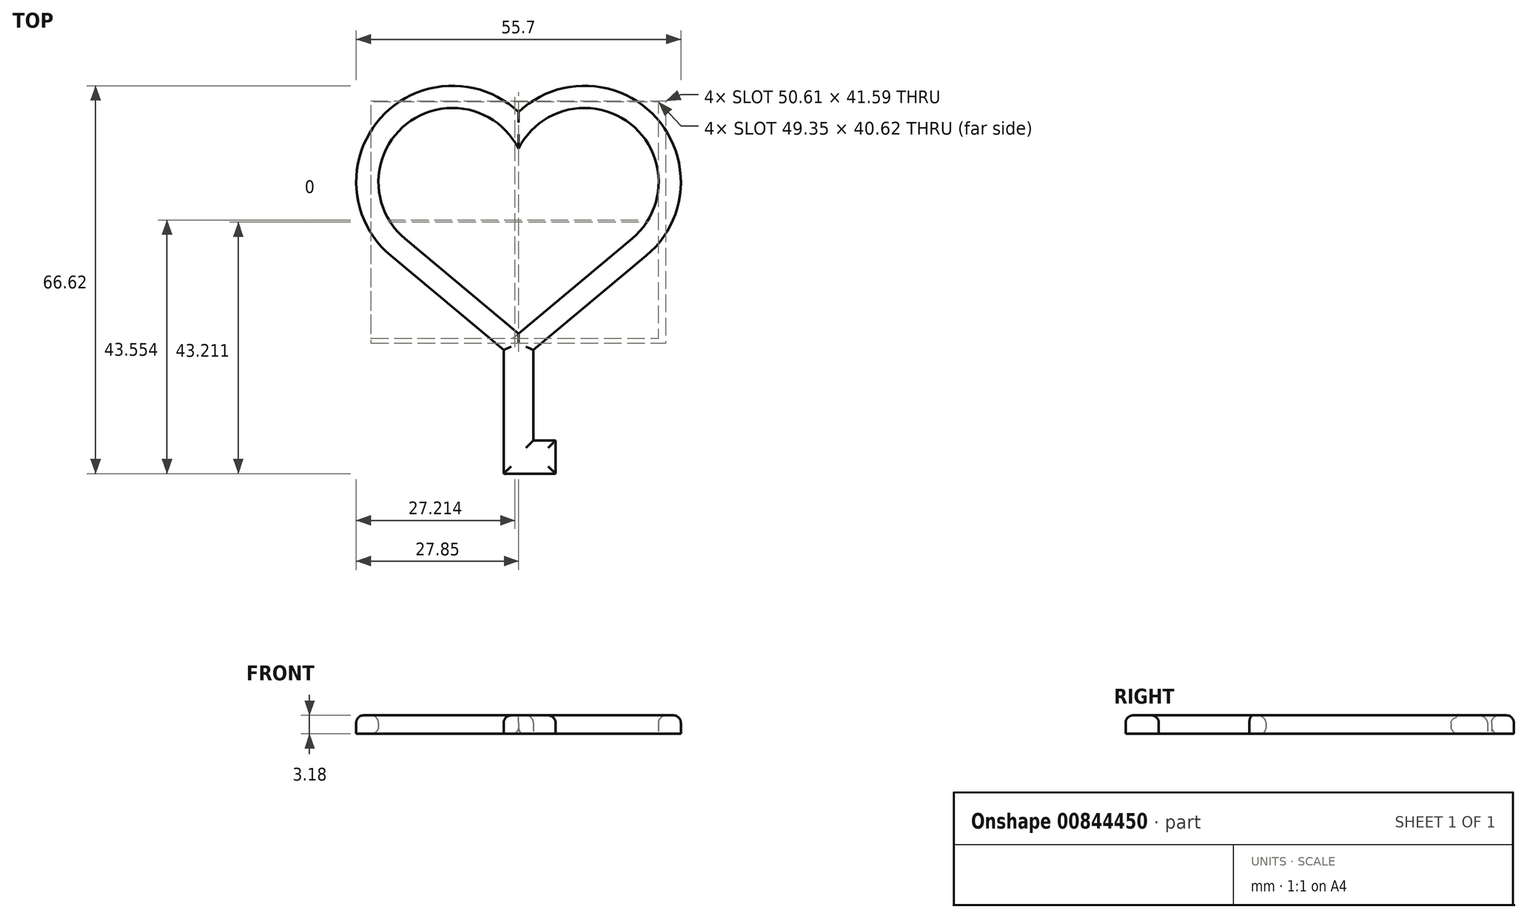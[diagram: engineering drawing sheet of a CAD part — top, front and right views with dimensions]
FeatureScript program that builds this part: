
annotation { "Feature Type Name" : "Feature", "Feature Type Description" : "" }
export const myFeature = defineFeature(function(context is Context, id is Id, definition is map)
    precondition{}
    {
        {
            var Q0;
            Q0=qCreatedBy(makeId("Top.planeOp"),FACE);
            var sketch = newSketch(context, id + "F0", { "sketchPlane" : qUnion([Q0])});
            skLineSegment(sketch, "E0", {"start": v(0, 0) * mm, "end": v(-19.49, 16.3) * mm});
            skLineSegment(sketch, "E1", {"start": v(0, 0) * mm, "end": v(19.49, 16.3) * mm});
            skArc(sketch, "E2", {"start": v(-19.49, 16.3) * mm, "mid": v(-19.23, 35.98) * mm, "end": v(0, 31.75) * mm});
            skArc(sketch, "E3", {"start": v(19.49, 16.3) * mm, "mid": v(19.23, 35.98) * mm, "end": v(0, 31.75) * mm});
            skLineSegment(sketch, "E4", {"start": v(0, 0) * mm, "end": v(0, 31.75) * mm, "construction": true});
            skLineSegment(sketch, "E5", {"start": v(-2.54, -2.84) * mm, "end": v(-2.54, -18.38) * mm});
            skLineSegment(sketch, "E6", {"start": v(-2.54, -24.07) * mm, "end": v(2.54, -24.07) * mm});
            skLineSegment(sketch, "E7", {"start": v(2.54, -18.38) * mm, "end": v(2.54, -2.84) * mm});
            skLineSegment(sketch, "E8.bottom", {"start": v(2.54, -24.07) * mm, "end": v(6.35, -24.07) * mm});
            skLineSegment(sketch, "E8.top", {"start": v(2.54, -18.38) * mm, "end": v(6.35, -18.38) * mm});
            skLineSegment(sketch, "E8.left", {"start": v(-2.54, -24.07) * mm, "end": v(-2.54, -18.38) * mm});
            skLineSegment(sketch, "E8.right", {"start": v(6.35, -24.07) * mm, "end": v(6.35, -18.38) * mm});
            skArc(sketch, "E9.0", {"start": v(-21.93, 13.37) * mm, "mid": v(-23.68, 37) * mm, "end": v(0, 38.03) * mm});
            skLineSegment(sketch, "E9.1", {"start": v(-2.54, -2.84) * mm, "end": v(-21.93, 13.37) * mm});
            skLineSegment(sketch, "E9.2", {"start": v(2.54, -2.84) * mm, "end": v(21.93, 13.37) * mm});
            skArc(sketch, "E9.3", {"start": v(21.93, 13.37) * mm, "mid": v(23.68, 37) * mm, "end": v(0, 38.03) * mm});
            skSolve(sketch);
        }
        {
            var Q0;
            Q0 = qSketchRegion(id + "F0", true);
            var Q1;
            Q1=makeQuery(id+"F0.imprint","IMPRINT",FACE,{"disambiguationData":[TD([[makeQuery(id+"F0.imprint","IMPRINT",EDGE,{"derivedFrom":sQuery(id+"F0.wireOp",EDGE,"E0")}),1.0]])]});
            extrude(context, id + "F1", {"entities" : qUnion([Q0, Q1]), "depth" : 3.17 * mm, "offsetDistance" : 25.4 * mm});
        }
        {
            var Q0;
            Q0=makeQuery(id+"F1.opExtrude","CAP_EDGE",EDGE,{"disambiguationData":[OSD([sQuery(id+"F0.wireOp",EDGE,"E9.1")])],"isStart":false});
            var Q1;
            Q1=makeQuery(id+"F1.opExtrude","CAP_EDGE",EDGE,{"disambiguationData":[OSD([sQuery(id+"F0.wireOp",EDGE,"E9.0")])],"isStart":false});
            var Q2;
            Q2=makeQuery(id+"F1.opExtrude","CAP_EDGE",EDGE,{"disambiguationData":[OSD([sQuery(id+"F0.wireOp",EDGE,"E9.3")])],"isStart":false});
            var Q3;
            Q3=makeQuery(id+"F1.opExtrude","CAP_EDGE",EDGE,{"disambiguationData":[OSD([sQuery(id+"F0.wireOp",EDGE,"E9.2")])],"isStart":false});
            var Q4;
            Q4=makeQuery(id+"F1.opExtrude","CAP_EDGE",EDGE,{"disambiguationData":[OSD([sQuery(id+"F0.wireOp",EDGE,"E5"),sQuery(id+"F0.wireOp",EDGE,"E8.left")])],"isStart":false});
            var Q5;
            Q5=makeQuery(id+"F1.opExtrude","CAP_EDGE",EDGE,{"disambiguationData":[OSD([sQuery(id+"F0.wireOp",EDGE,"E7")])],"isStart":false});
            var Q6;
            Q6=makeQuery(id+"F1.opExtrude","CAP_EDGE",EDGE,{"disambiguationData":[OSD([sQuery(id+"F0.wireOp",EDGE,"E0")])],"isStart":true});
            var Q7;
            Q7=makeQuery(id+"F1.opExtrude","CAP_EDGE",EDGE,{"disambiguationData":[OSD([sQuery(id+"F0.wireOp",EDGE,"E2")])],"isStart":false});
            var Q8;
            Q8=makeQuery(id+"F1.opExtrude","CAP_EDGE",EDGE,{"disambiguationData":[OSD([sQuery(id+"F0.wireOp",EDGE,"E3")])],"isStart":false});
            var Q9;
            Q9=makeQuery(id+"F1.opExtrude","CAP_EDGE",EDGE,{"disambiguationData":[OSD([sQuery(id+"F0.wireOp",EDGE,"E8.top")])],"isStart":false});
            var Q10;
            Q10=makeQuery(id+"F1.opExtrude","CAP_EDGE",EDGE,{"disambiguationData":[OSD([sQuery(id+"F0.wireOp",EDGE,"E8.right")])],"isStart":false});
            var Q11;
            Q11=makeQuery(id+"F1.opExtrude","CAP_EDGE",EDGE,{"disambiguationData":[OSD([sQuery(id+"F0.wireOp",EDGE,"E6"),sQuery(id+"F0.wireOp",EDGE,"E8.bottom")])],"isStart":false});
            fillet(context, id + "F2", {"entities" : qUnion([Q0, Q1, Q2, Q3, Q4, Q5, Q6, Q7, Q8, Q9, Q10, Q11]), "radius" : 1.27 * mm, "tangentPropagation" : true, "allowEdgeOverflow" : false});
        }
    });
